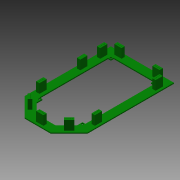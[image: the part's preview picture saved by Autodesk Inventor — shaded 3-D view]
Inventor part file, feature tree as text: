
AUTODESK INVENTOR PART (.ipt)
format: ipt  version: 2015 (Build 190159000, 159)  size: 365,056 bytes
history: native  units: mm
features: extrude x4, sketch x3
ambient origin geometry x8: Origin, YZ Plane, XZ Plane, XY Plane, X Axis, Y Axis, Z Axis, Center Point
bodies: Solid1 (feature_tree)
feature tree (7):
  sketch  "Sketch1"  dims[d521=15.113mm d522=15.113mm d523=15.113mm d551=5.76mm d552=2.54mm]
  extrude  "Extrusion1"  Depth=5.76mm
  extrude  "Extrusion2"  Depth=1.0mm
  extrude  "Extrusion4"  Depth=1.7mm
  extrude  "Extrusion6"  Depth=1.7mm
  sketch  "Sketch2"  dims[d556=1.0mm d557=1.0mm]
  sketch  "Sketch4"  dims[d558=2.54mm d560=1.27mm d561=2.54mm d563=2.54mm d564=0.64mm d565=0.64mm d566=0.64mm d567=0.64mm d568=0.64mm d569=0.64mm d570=0.64mm d571=0.64mm d572=1.7mm d573=0.0mm d574=17.8mm d575=0.0mm d578=1.09mm d579=22.33mm d580=16.1mm d581=0.0mm d596=5.0mm d597=5.0mm d599=5.0mm d600=5.0mm d602=10.0mm d603=7.071068mm d604=3.5mm d605=2.5mm d606=2.5mm d607=1.7mm d608=0.0mm d609=3.5mm d610=2.5mm d611=2.5mm]
